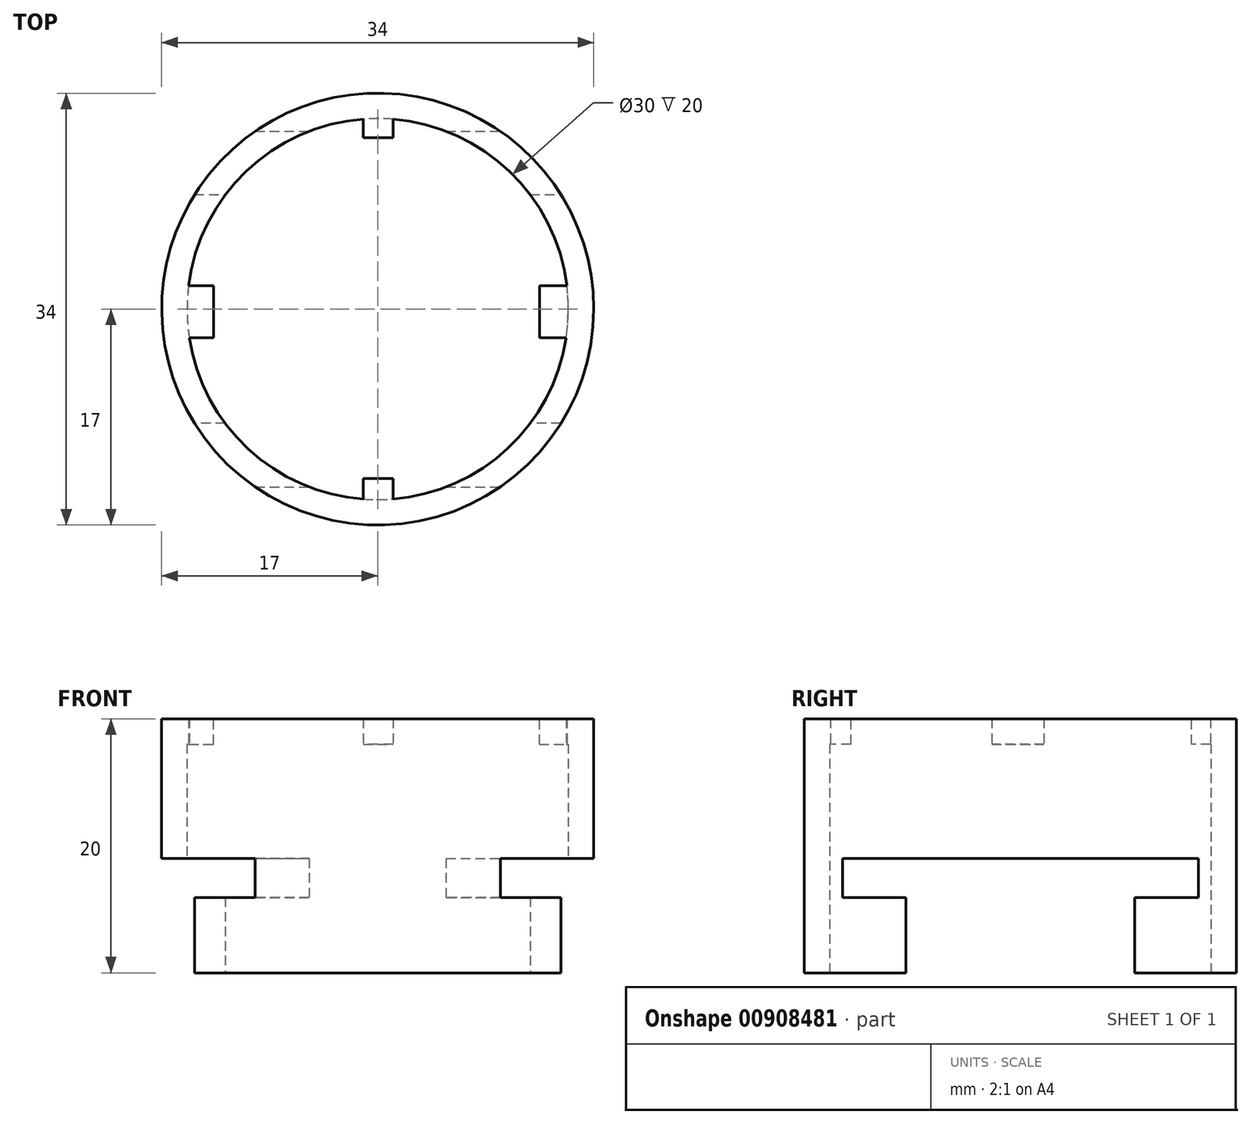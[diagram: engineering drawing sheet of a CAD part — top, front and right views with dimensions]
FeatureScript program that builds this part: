
annotation { "Feature Type Name" : "Feature", "Feature Type Description" : "" }
export const myFeature = defineFeature(function(context is Context, id is Id, definition is map)
    precondition{}
    {
        {
            var Q0;
            Q0=qCreatedBy(makeId("Top.planeOp"),FACE);
            var sketch = newSketch(context, id + "F0", { "sketchPlane" : qUnion([Q0])});
            skCircle(sketch, "E0", {"center": v(0, 0) * mm, "radius": 15 * mm});
            skCircle(sketch, "E1", {"center": v(0, 0) * mm, "radius": 17 * mm});
            skSolve(sketch);
        }
        {
            var Q0;
            Q0=makeQuery(id+"F0.imprint","IMPRINT",FACE,{"disambiguationData":[TD([[makeQuery(id+"F0.imprint","IMPRINT",EDGE,{"derivedFrom":sQuery(id+"F0.wireOp",EDGE,"E0")}),-1.0]])]});
            extrude(context, id + "F1", {"entities" : qUnion([Q0]), "depth" : 20 * mm, "offsetDistance" : 25 * mm});
        }
        {
            var Q0;
            Q0=qCreatedBy(makeId("Right.planeOp"),FACE);
            var sketch = newSketch(context, id + "F2", { "sketchPlane" : qUnion([Q0])});
            skLineSegment(sketch, "E2", {"start": v(-9, -6.12) * mm, "end": v(-9, 5.94) * mm});
            skLineSegment(sketch, "E3", {"start": v(-9, 5.94) * mm, "end": v(-14, 5.94) * mm});
            skLineSegment(sketch, "E4", {"start": v(-14, 5.94) * mm, "end": v(-14, 9) * mm});
            skLineSegment(sketch, "E5", {"start": v(-14, 9) * mm, "end": v(14, 9) * mm});
            skLineSegment(sketch, "E6", {"start": v(14, 9) * mm, "end": v(14, 5.94) * mm});
            skLineSegment(sketch, "E7", {"start": v(14, 5.94) * mm, "end": v(9, 5.94) * mm});
            skLineSegment(sketch, "E8", {"start": v(9, 5.94) * mm, "end": v(9, -5.76) * mm});
            skLineSegment(sketch, "E9", {"start": v(9, -5.76) * mm, "end": v(-9, -6.12) * mm});
            skSolve(sketch);
        }
        {
            var Q0;
            Q0=makeQuery(id+"F2.imprint","IMPRINT",FACE,{"disambiguationData":[TD([[makeQuery(id+"F2.imprint","IMPRINT",EDGE,{"derivedFrom":sQuery(id+"F2.wireOp",EDGE,"E2")}),-1.0]])]});
            extrude(context, id + "F3", {"entities" : qUnion([Q0]), "operationType" : NewBodyOperationType.REMOVE, "endBound" : BoundingType.SYMMETRIC, "oppositeDirection" : true, "depth" : 50 * mm, "offsetDistance" : 25 * mm});
        }
        {
            var Q0;
            Q0=makeQuery(id+"F1.opExtrude","CAP_FACE",FACE,{"disambiguationData":[OSD([sQuery(id+"F0.wireOp",EDGE,"E0"),sQuery(id+"F0.wireOp",EDGE,"E1")])],"isStart":false});
            var sketch = newSketch(context, id + "F4", { "sketchPlane" : qUnion([Q0])});
            skLineSegment(sketch, "E10.bottom", {"start": v(-16.42, 1.84) * mm, "end": v(16.6, 1.84) * mm});
            skLineSegment(sketch, "E10.top", {"start": v(-16.42, -2.24) * mm, "end": v(16.6, -2.24) * mm});
            skLineSegment(sketch, "E10.left", {"start": v(-16.42, 1.84) * mm, "end": v(-16.42, -2.24) * mm});
            skLineSegment(sketch, "E10.right", {"start": v(16.6, 1.84) * mm, "end": v(16.6, -2.24) * mm});
            skLineSegment(sketch, "E11.bottom", {"start": v(-12.92, 1.84) * mm, "end": v(12.73, 1.84) * mm});
            skLineSegment(sketch, "E11.top", {"start": v(-12.92, -2.24) * mm, "end": v(12.73, -2.24) * mm});
            skLineSegment(sketch, "E11.left", {"start": v(-12.92, 1.84) * mm, "end": v(-12.92, -2.24) * mm});
            skLineSegment(sketch, "E11.right", {"start": v(12.73, 1.84) * mm, "end": v(12.73, -2.24) * mm});
            skSolve(sketch);
        }
        {
            var Q0;
            {var subQ0=sQuery(id+"F4.wireOp",EDGE,"E10.left");Q0=makeQuery(id+"F4.imprint","IMPRINT",FACE,{"disambiguationData":[TD([[makeQuery(id+"F4.imprint","IMPRINT",EDGE,{"derivedFrom":subQ0}),1.0]])]});}
            var Q1;
            {var subQ0=sQuery(id+"F4.wireOp",EDGE,"E11.left");Q1=makeQuery(id+"F4.imprint","IMPRINT",FACE,{"disambiguationData":[TD([[makeQuery(id+"F4.imprint","IMPRINT",EDGE,{"derivedFrom":subQ0}),-1.0]])]});}
            var Q2;
            {var subQ0=sQuery(id+"F4.wireOp",EDGE,"E11.right");Q2=makeQuery(id+"F4.imprint","IMPRINT",FACE,{"disambiguationData":[TD([[makeQuery(id+"F4.imprint","IMPRINT",EDGE,{"derivedFrom":subQ0}),1.0]])]});}
            var Q3;
            {var subQ0=sQuery(id+"F4.wireOp",EDGE,"E10.right");Q3=makeQuery(id+"F4.imprint","IMPRINT",FACE,{"disambiguationData":[TD([[makeQuery(id+"F4.imprint","IMPRINT",EDGE,{"derivedFrom":subQ0}),-1.0]])]});}
            extrude(context, id + "F5", {"entities" : qUnion([Q0, Q1, Q2, Q3]), "operationType" : NewBodyOperationType.ADD, "oppositeDirection" : true, "depth" : 2 * mm, "offsetDistance" : 25 * mm});
        }
        {
            var Q0;
            {var subQ0=sQuery(id+"F4.wireOp",EDGE,"E10.top");var subQ1=sQuery(id+"F4.wireOp",EDGE,"E10.bottom");Q0=makeQuery(id+"F5.boolean.opBoolean","MERGE",FACE,{"derivedFrom":[makeQuery(id+"F1.opExtrude","CAP_FACE",FACE,{"disambiguationData":[OSD([sQuery(id+"F0.wireOp",EDGE,"E0"),sQuery(id+"F0.wireOp",EDGE,"E1")])],"isStart":false}),makeQuery(id+"F5.opExtrude","CAP_FACE",FACE,{"disambiguationData":[OSD([subQ1,subQ0,sQuery(id+"F4.wireOp",EDGE,"E10.left"),sQuery(id+"F4.wireOp",EDGE,"E11.left")])],"isStart":true}),makeQuery(id+"F5.opExtrude","CAP_FACE",FACE,{"disambiguationData":[OSD([subQ1,subQ0,sQuery(id+"F4.wireOp",EDGE,"E10.right"),sQuery(id+"F4.wireOp",EDGE,"E11.right")])],"isStart":true})]});}
            var sketch = newSketch(context, id + "F6", { "sketchPlane" : qUnion([Q0])});
            skLineSegment(sketch, "E12.bottom", {"start": v(-1.14, 16.1) * mm, "end": v(1.2, 16.1) * mm});
            skLineSegment(sketch, "E12.top", {"start": v(-1.14, -15.86) * mm, "end": v(1.2, -15.86) * mm});
            skLineSegment(sketch, "E12.left", {"start": v(-1.14, 16.1) * mm, "end": v(-1.14, -15.86) * mm});
            skLineSegment(sketch, "E12.right", {"start": v(1.2, 16.1) * mm, "end": v(1.2, -15.86) * mm});
            skLineSegment(sketch, "E13.bottom", {"start": v(-1.14, 13.48) * mm, "end": v(1.2, 13.48) * mm});
            skLineSegment(sketch, "E13.top", {"start": v(-1.14, -13.34) * mm, "end": v(1.2, -13.34) * mm});
            skLineSegment(sketch, "E13.left", {"start": v(-1.14, 13.48) * mm, "end": v(-1.14, -13.34) * mm});
            skLineSegment(sketch, "E13.right", {"start": v(1.2, 13.48) * mm, "end": v(1.2, -13.34) * mm});
            skSolve(sketch);
        }
        {
            var Q0;
            {var subQ0=sQuery(id+"F6.wireOp",EDGE,"E13.bottom");Q0=makeQuery(id+"F6.imprint","IMPRINT",FACE,{"disambiguationData":[TD([[makeQuery(id+"F6.imprint","IMPRINT",EDGE,{"derivedFrom":subQ0}),1.0]])]});}
            var Q1;
            {var subQ0=sQuery(id+"F6.wireOp",EDGE,"E12.bottom");Q1=makeQuery(id+"F6.imprint","IMPRINT",FACE,{"disambiguationData":[TD([[makeQuery(id+"F6.imprint","IMPRINT",EDGE,{"derivedFrom":subQ0}),-1.0]])]});}
            var Q2;
            {var subQ0=sQuery(id+"F6.wireOp",EDGE,"E12.top");Q2=makeQuery(id+"F6.imprint","IMPRINT",FACE,{"disambiguationData":[TD([[makeQuery(id+"F6.imprint","IMPRINT",EDGE,{"derivedFrom":subQ0}),1.0]])]});}
            var Q3;
            {var subQ0=sQuery(id+"F6.wireOp",EDGE,"E13.top");Q3=makeQuery(id+"F6.imprint","IMPRINT",FACE,{"disambiguationData":[TD([[makeQuery(id+"F6.imprint","IMPRINT",EDGE,{"derivedFrom":subQ0}),-1.0]])]});}
            extrude(context, id + "F7", {"entities" : qUnion([Q0, Q1, Q2, Q3]), "operationType" : NewBodyOperationType.ADD, "oppositeDirection" : true, "depth" : 2 * mm, "offsetDistance" : 25 * mm});
        }
    });
